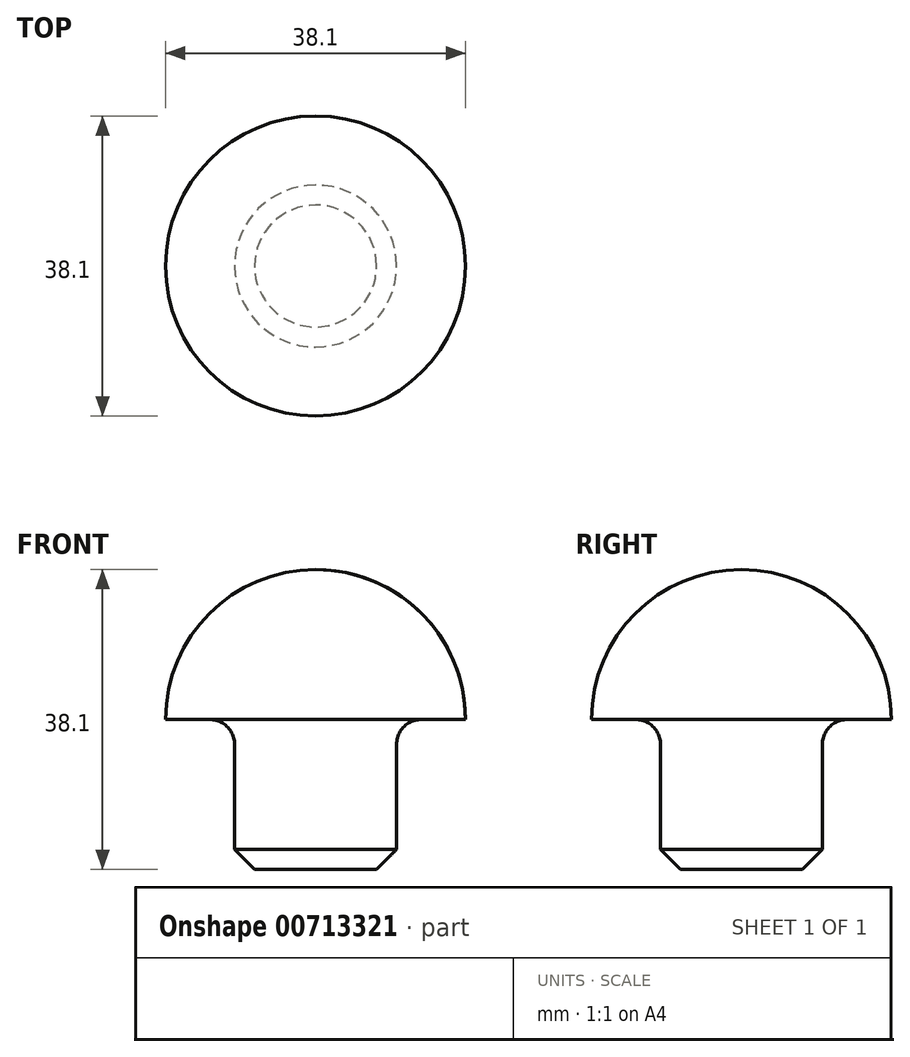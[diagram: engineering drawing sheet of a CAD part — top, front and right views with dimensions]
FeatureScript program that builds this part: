
annotation { "Feature Type Name" : "Feature", "Feature Type Description" : "" }
export const myFeature = defineFeature(function(context is Context, id is Id, definition is map)
    precondition{}
    {
        {
            var Q0;
            Q0=qCreatedBy(makeId("Front.planeOp"),FACE);
            var sketch = newSketch(context, id + "F0", { "sketchPlane" : qUnion([Q0])});
            skLineSegment(sketch, "E0", {"start": v(0, -19.05) * mm, "end": v(10.29, -19.05) * mm});
            skLineSegment(sketch, "E1", {"start": v(10.29, -19.05) * mm, "end": v(10.29, 0) * mm});
            skLineSegment(sketch, "E2", {"start": v(10.29, 0) * mm, "end": v(19.05, 0) * mm});
            skLineSegment(sketch, "E3", {"start": v(19.05, 0) * mm, "end": v(19.05, 0) * mm});
            skArc(sketch, "E4", {"start": v(19.05, 0) * mm, "mid": v(13.47, 13.47) * mm, "end": v(0, 19.05) * mm});
            skPoint(sketch, "E5.orphan", {"position": v(0, 40.23) * mm});
            skLineSegment(sketch, "E6", {"start": v(0, -19.05) * mm, "end": v(0, 19.05) * mm});
            skSolve(sketch);
        }
        {
            var Q0;
            Q0=qCreatedBy(makeId("Front.planeOp"),FACE);
            var sketch = newSketch(context, id + "F1", { "sketchPlane" : qUnion([Q0])});
            skLineSegment(sketch, "E7", {"start": v(0, 31) * mm, "end": v(0, -34.2) * mm, "construction": true});
            skSolve(sketch);
        }
        {
            var Q0;
            Q0=makeQuery(id+"F0.imprint","IMPRINT",FACE,{"disambiguationData":[TD([[makeQuery(id+"F0.imprint","IMPRINT",EDGE,{"derivedFrom":sQuery(id+"F0.wireOp",EDGE,"E0")}),1.0]])]});
            var Q1;
            Q1=sQuery(id+"F1.wireOp",EDGE,"E7");
            revolve(context, id + "F2", {"surfaceOperationType" : NewSurfaceOperationType.NEW, "entities" : qUnion([Q0]), "axis" : qUnion([Q1]), "revolveType" : RevolveType.FULL});
        }
        {
            var Q0;
            Q0=makeQuery(id+"F2.opRevolve","SWEPT_EDGE",EDGE,{"disambiguationData":[OSD([sQuery(id+"F0.wireOp",EDGE,"E1"),sQuery(id+"F0.wireOp",EDGE,"E2")])]});
            fillet(context, id + "F3", {"entities" : qUnion([Q0]), "radius" : 3.17 * mm, "tangentPropagation" : true, "allowEdgeOverflow" : false});
        }
        {
            var Q0;
            Q0=makeQuery(id+"F2.opRevolve","SWEPT_EDGE",EDGE,{"disambiguationData":[OSD([sQuery(id+"F0.wireOp",EDGE,"E0"),sQuery(id+"F0.wireOp",EDGE,"E1")])]});
            chamfer(context, id + "F4", {"entities" : qUnion([Q0]), "width" : 2.54 * mm, "tangentPropagation" : true});
        }
    });
